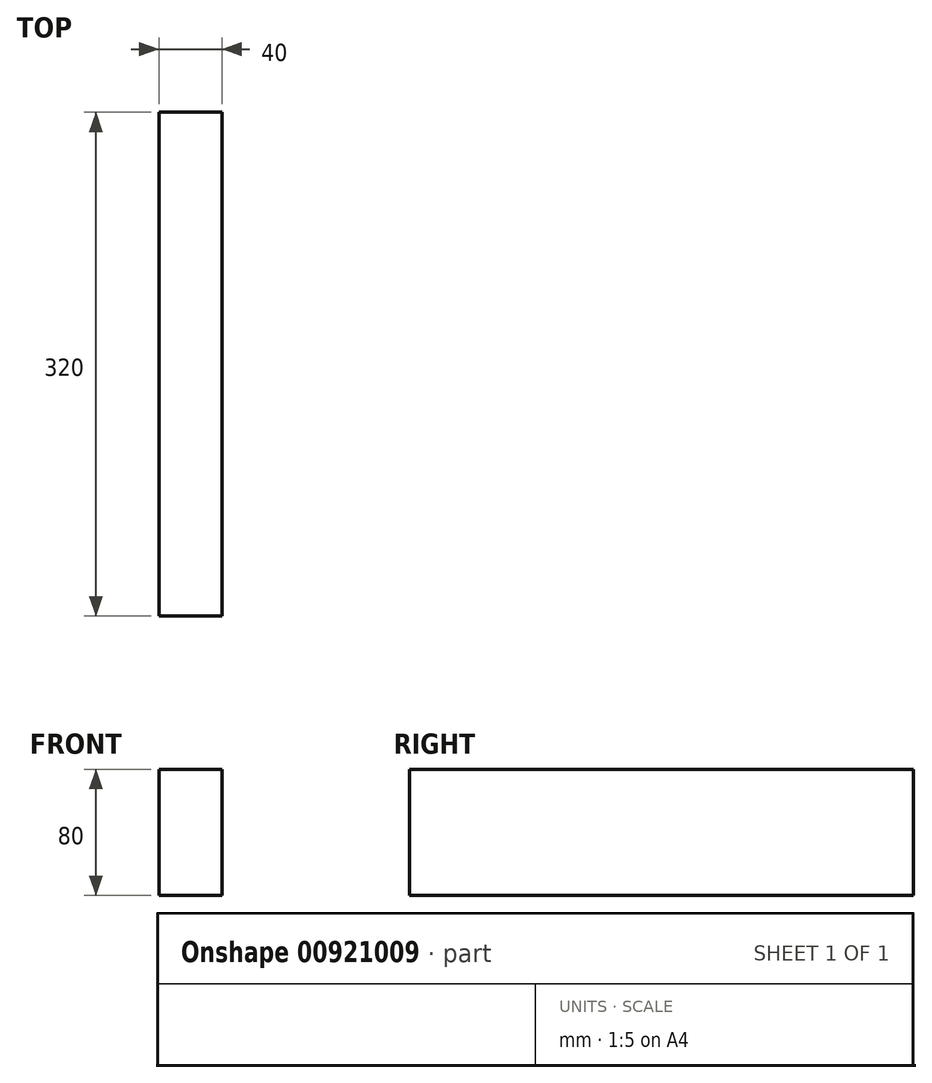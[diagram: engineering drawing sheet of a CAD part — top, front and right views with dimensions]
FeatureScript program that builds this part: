
annotation { "Feature Type Name" : "Feature", "Feature Type Description" : "" }
export const myFeature = defineFeature(function(context is Context, id is Id, definition is map)
    precondition{}
    {
        {
            var Q0;
            Q0=qCreatedBy(makeId("Top.planeOp"),FACE);
            var sketch = newSketch(context, id + "F0", { "sketchPlane" : qUnion([Q0])});
            skLineSegment(sketch, "E0.bottom", {"start": v(-160, 40) * mm, "end": v(160, 40) * mm});
            skLineSegment(sketch, "E0.top", {"start": v(-160, -40) * mm, "end": v(160, -40) * mm});
            skLineSegment(sketch, "E0.left", {"start": v(-160, 40) * mm, "end": v(-160, -40) * mm});
            skLineSegment(sketch, "E0.right", {"start": v(160, 40) * mm, "end": v(160, -40) * mm});
            skPoint(sketch, "E0.middle", {"position": v(0, 0) * mm});
            skSolve(sketch);
        }
        {
            var Q0;
            Q0=makeQuery(id+"F0.imprint","IMPRINT",FACE,{"disambiguationData":[TD([[makeQuery(id+"F0.imprint","IMPRINT",EDGE,{"derivedFrom":sQuery(id+"F0.wireOp",EDGE,"E0.bottom")}),-1.0]])]});
            extrude(context, id + "F1", {"entities" : qUnion([Q0]), "endBound" : BoundingType.SYMMETRIC, "depth" : 40 * mm, "offsetDistance" : 25 * mm});
        }
        {
            var Q0;
            Q0=makeQuery(id+"F1.opExtrude","SWEPT_BODY",BODY,{"disambiguationData":[OSD([sQuery(id+"F0.wireOp",EDGE,"E0.bottom"),sQuery(id+"F0.wireOp",EDGE,"E0.top"),sQuery(id+"F0.wireOp",EDGE,"E0.left"),sQuery(id+"F0.wireOp",EDGE,"E0.right")])]});
            var Q1;
            Q1=makeQuery(id+"F1.opExtrude","CAP_EDGE",EDGE,{"disambiguationData":[OSD([sQuery(id+"F0.wireOp",EDGE,"E0.top")])],"isStart":true});
            transform(context, id + "F2", {"entities" : qUnion([Q0]), "transformType" : TransformType.ROTATION, "transformAxis" : qUnion([Q1]), "angle" : 90 * degree, "makeCopy" : false});
        }
        {
            var Q0;
            Q0=makeQuery(id+"F1.opExtrude","SWEPT_BODY",BODY,{"disambiguationData":[OSD([sQuery(id+"F0.wireOp",EDGE,"E0.bottom"),sQuery(id+"F0.wireOp",EDGE,"E0.top"),sQuery(id+"F0.wireOp",EDGE,"E0.left"),sQuery(id+"F0.wireOp",EDGE,"E0.right")])]});
            var Q1;
            Q1=makeQuery(id+"F1.opExtrude","CAP_EDGE",EDGE,{"disambiguationData":[OSD([sQuery(id+"F0.wireOp",EDGE,"E0.right")])],"isStart":true});
            transform(context, id + "F3", {"entities" : qUnion([Q0]), "transformType" : TransformType.ROTATION, "transformAxis" : qUnion([Q1]), "angle" : 90 * degree, "makeCopy" : false});
        }
    });
